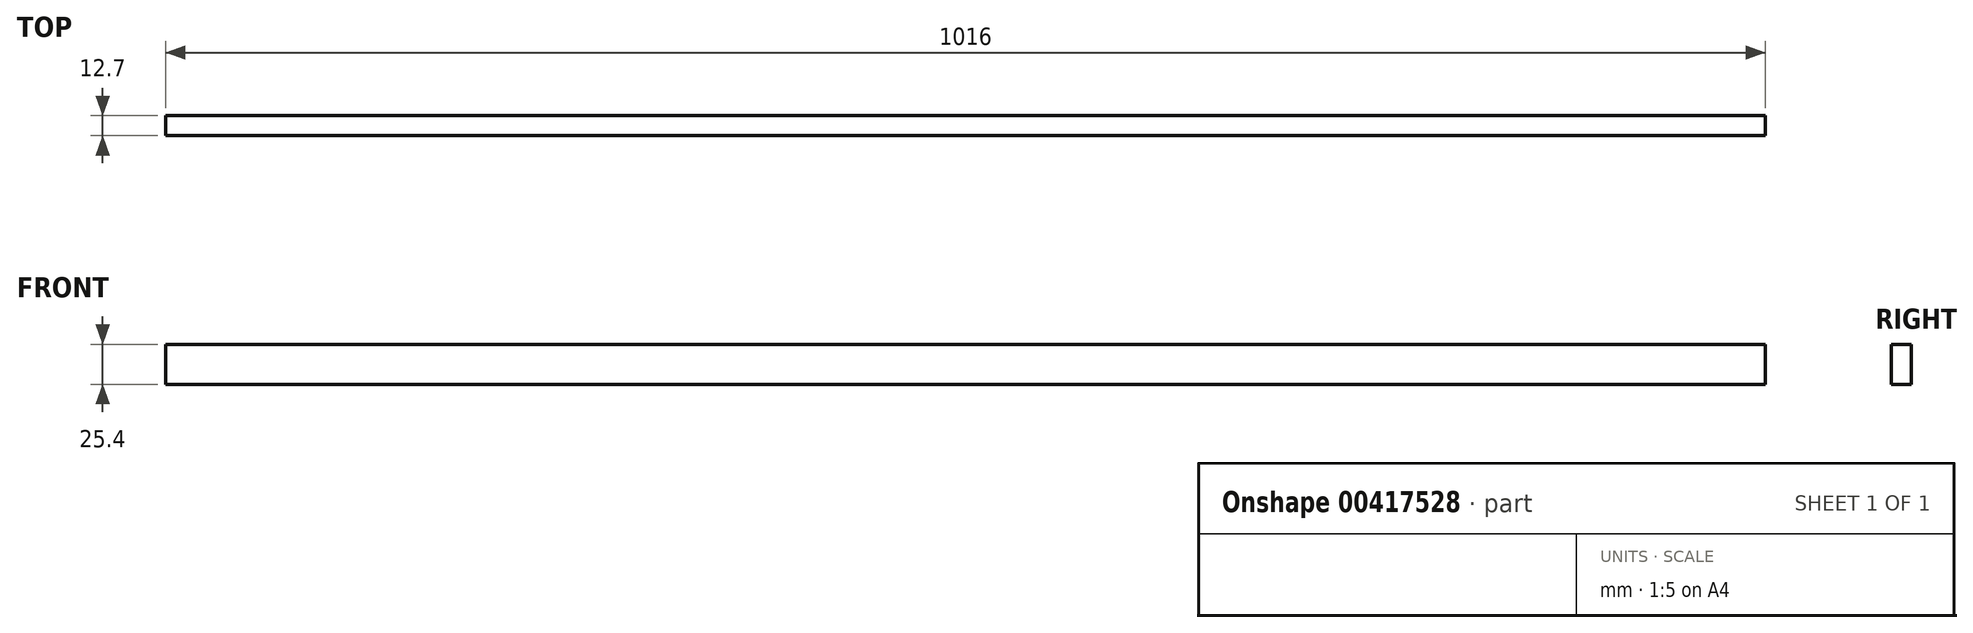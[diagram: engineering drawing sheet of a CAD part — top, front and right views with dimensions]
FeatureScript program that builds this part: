
annotation { "Feature Type Name" : "Feature", "Feature Type Description" : "" }
export const myFeature = defineFeature(function(context is Context, id is Id, definition is map)
    precondition{}
    {
        {
            var Q0;
            Q0=qCreatedBy(makeId("Front.planeOp"),FACE);
            var sketch = newSketch(context, id + "F0", { "sketchPlane" : qUnion([Q0])});
            skLineSegment(sketch, "E0.bottom", {"start": v(-508, 12.7) * mm, "end": v(508, 12.7) * mm});
            skLineSegment(sketch, "E0.top", {"start": v(-508, -12.7) * mm, "end": v(508, -12.7) * mm});
            skLineSegment(sketch, "E0.left", {"start": v(-508, 12.7) * mm, "end": v(-508, -12.7) * mm});
            skLineSegment(sketch, "E0.right", {"start": v(508, 12.7) * mm, "end": v(508, -12.7) * mm});
            skPoint(sketch, "E0.middle", {"position": v(0, 0) * mm});
            skSolve(sketch);
        }
        {
            var Q0;
            Q0=qSketchRegion(id+"F0",true);
            extrude(context, id + "F1", {"entities" : qUnion([Q0]), "depth" : 12.7 * mm});
        }
    });
